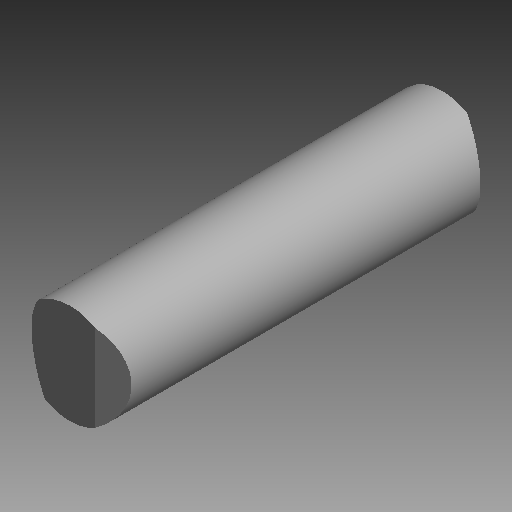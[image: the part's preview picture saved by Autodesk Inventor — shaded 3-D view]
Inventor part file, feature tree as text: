
AUTODESK INVENTOR PART (.ipt)
format: ipt  version: 2019 (Build 230136000, 136)  size: 110,592 bytes
history: native  units: mm (DEFAULTED — no unit token found)
features: other x14, sketch x5, extrude x4, revolve x1
ambient origin geometry x8: Origin, YZ Plane, XZ Plane, XY Plane, X Axis, Y Axis, Z Axis, Center Point
bodies: Solid1 (feature_tree), Body2_1_XY (feature_tree), Body2_1_YZ (feature_tree), Body2_1_ZX (feature_tree), Body2_1_X (feature_tree), Body2_1_Y (feature_tree), Body2_1_Z (feature_tree), Body2_1_Center (feature_tree)
feature tree (24):
  revolve  "Revolution1"  [1 undecoded]
  extrude  "Extrusion1"  Depth=3.28mm TaperAngle=0.0deg
  extrude  "Extrusion2"  [1 undecoded]
  extrude  "Extrusion3"  [1 undecoded]
  extrude  "Extrusion4"  [1 undecoded]
  other  "for_pin_XY"
  other  "for_pin_YZ"
  other  "for_pin_ZX"
  other  "for_pin_X"
  other  "for_pin_Y"
  other  "for_pin_Z"
  other  "for_pin_Center"
  other  "to_dummy_1_XY"
  other  "to_dummy_1_YZ"
  other  "to_dummy_1_ZX"
  other  "to_dummy_1_X"
  other  "to_dummy_1_Y"
  other  "to_dummy_1_Z"
  other  "to_dummy_1_Center"
  sketch  "Sketch_1"  dims[d0=360.0deg d1=3.28mm d2=0.0mm]
  sketch  "Sketch_7"  dims[d3=3.28mm d4=0.0mm d5=3.28mm d6=0.0mm]
  sketch  "Sketch_8"  dims[d7=3.28mm d8=0.0mm]
  sketch  "Sketch_9"
  sketch  "Sketch_10"
note: 4 required parameter values undecoded (feature->parameter linkage not recoverable at this tier; creation-order binding heuristic only, values carry confidence <= 0.55)